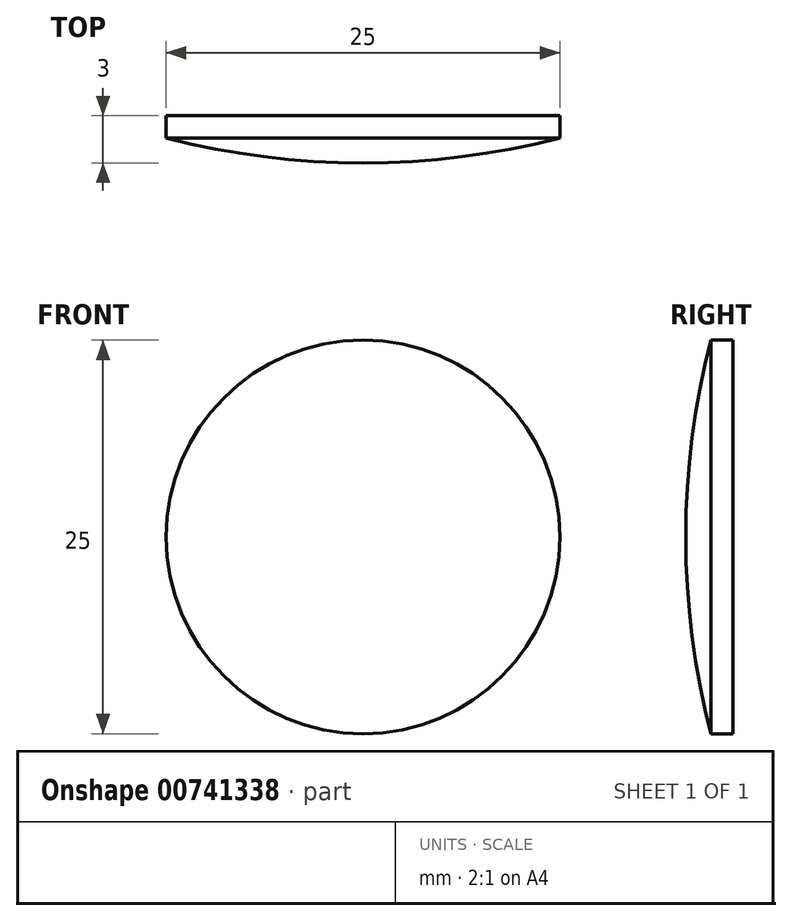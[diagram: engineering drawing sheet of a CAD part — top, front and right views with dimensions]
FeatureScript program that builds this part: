
annotation { "Feature Type Name" : "Feature", "Feature Type Description" : "" }
export const myFeature = defineFeature(function(context is Context, id is Id, definition is map)
    precondition{}
    {
        {
            var Q0;
            Q0=qCreatedBy(makeId("Top.planeOp"),FACE);
            var sketch = newSketch(context, id + "F0", { "sketchPlane" : qUnion([Q0])});
            skCircle(sketch, "E0", {"center": v(0, 0) * mm, "radius": 50 * mm});
            skLineSegment(sketch, "E1", {"start": v(0, 0) * mm, "end": v(-64.9, 0) * mm});
            skLineSegment(sketch, "E2", {"start": v(-64.9, 0) * mm, "end": v(61.66, 0) * mm});
            skSolve(sketch);
        }
        {
            var Q0;
            {var subQ0=sQuery(id+"F0.wireOp",EDGE,"E2");var subQ4=makeQuery(id+"F0.imprint","IMPRINT",VERTEX,{"derivedFrom":subQ0});Q0=makeQuery(id+"F0.imprint","IMPRINT",FACE,{"disambiguationData":[TD([[makeQuery(id+"F0.imprint","IMPRINT",EDGE,{"disambiguationData":[TD([[subQ4,1.0]])],"derivedFrom":subQ0}),-1.0]])]});}
            var Q1;
            Q1=sQuery(id+"F0.wireOp",EDGE,"E2");
            revolve(context, id + "F1", {"surfaceOperationType" : NewSurfaceOperationType.NEW, "entities" : qUnion([Q0]), "axis" : qUnion([Q1]), "revolveType" : RevolveType.FULL});
        }
        {
            var Q0;
            Q0=qCreatedBy(makeId("Front.planeOp"),FACE);
            var sketch = newSketch(context, id + "F2", { "sketchPlane" : qUnion([Q0])});
            skCircle(sketch, "E3", {"center": v(0, 0) * mm, "radius": 12.5 * mm});
            skSolve(sketch);
        }
        {
            var Q0;
            Q0 = qSketchRegion(id + "F2", true);
            var Q1;
            Q1=makeQuery(id+"F1.opRevolve","SWEPT_FACE",FACE,{"disambiguationData":[OSD([sQuery(id+"F0.wireOp",EDGE,"E0")])]});
            extrude(context, id + "F3", {"entities" : qUnion([Q0]), "operationType" : NewBodyOperationType.INTERSECT, "endBound" : BoundingType.UP_TO_SURFACE, "depth" : 25 * mm, "endBoundEntityFace" : qUnion([Q1]), "offsetDistance" : 25 * mm});
        }
        {
            var Q0;
            Q0=qCreatedBy(makeId("Front.planeOp"),FACE);
            var sketch = newSketch(context, id + "F4", { "sketchPlane" : qUnion([Q0])});
            skCircle(sketch, "E4", {"center": v(0, 0) * mm, "radius": 25 * mm});
            skSolve(sketch);
        }
        {
            var Q0;
            Q0 = qSketchRegion(id + "F4", true);
            extrude(context, id + "F5", {"entities" : qUnion([Q0]), "operationType" : NewBodyOperationType.REMOVE, "depth" : 47 * mm, "offsetDistance" : 25 * mm});
        }
    });
